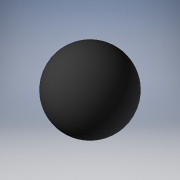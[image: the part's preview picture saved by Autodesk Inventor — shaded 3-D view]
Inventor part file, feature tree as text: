
AUTODESK INVENTOR PART (.ipt)
format: ipt  version: 2019 (Build 230136000, 136)  size: 135,168 bytes
history: native  units: mm
features: other x7, revolve x1, sketch x1
ambient origin geometry x8: Origin, YZ Plane, XZ Plane, XY Plane, X Axis, Y Axis, Z Axis, Center Point
bodies: Solid1 (feature_tree)
feature tree (9):
  revolve  "Revolution1"  [1 undecoded]
  other  "B_HW_XY"
  other  "B_HW_YZ"
  other  "B_HW_ZX"
  other  "B_HW_X"
  other  "B_HW_Y"
  other  "B_HW_Z"
  other  "B_HW_Center"
  sketch  "Sketch_1"  dims[d0=360.0deg]
note: 1 required parameter value undecoded (feature->parameter linkage not recoverable at this tier; creation-order binding heuristic only, values carry confidence <= 0.55)
